# Revit family: Verano_V150_Mallorca_GM_R21
name_source: partatom
category: Generic Models
units: mm (PartAtom-declared; Revit-internal decimal feet)

## family parameters
Always vertical = Yes
Can host rebar = No
Cut with Voids When Loaded = No
Part Type = Normal
Room Calculation Point = No
Round Connector Dimension = Use Diameter
Shared = No
Work Plane-Based = No

## types (4) — shared parameters
Description = Drop-arm awning
Electric Cntrl = Yes
Manual Cntrl = No
Manufacturer = Verano Systems
Maximal Width = 5000 mm  [stored 16.4042 ft]
Minimal Width = 1000 mm  [stored 3.28084 ft]
Model = V150 Mallorca
URL = https://verano.nl
zero-valued in all types: Default Elevation

## per-type parameters (varying)
| type | 1-1000 Projection | 2-1150 Projection | 3-1350 Projection | 4-1500 Projection | Height Constraint | TYPE |
| 2100 Projection | No | No | No | Yes | 1599 mm  [stored 5.24606 ft] | 4 |
| 1900 Projection | No | No | Yes | No | 1449 mm  [stored 4.75394 ft] | 3 |
| 1600 Projection | No | Yes | No | No | 1249 mm  [stored 4.09777 ft] | 2 |
| 1300 Projection | Yes | No | No | No | 1099 mm  [stored 3.60564 ft] | 1 |

note: [stored X ft] marks values corroborated as IEEE doubles in the binary element streams (Revit-internal decimal feet)

## geometry (parser evidence)
native form markers: Sweep x19
no freeform markers — native parametric forms only
